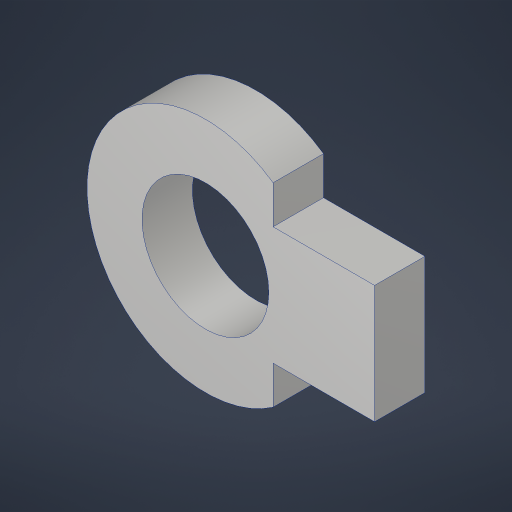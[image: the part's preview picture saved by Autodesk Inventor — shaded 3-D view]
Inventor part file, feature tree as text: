
AUTODESK INVENTOR PART (.ipt)
format: ipt  version: 2023.4 (Build 274418000, 418)  size: 176,640 bytes
history: native  units: in
note: dims shown in document units (in); Inventor stores cm internally (conversion verified against a paired STEP export)
features: extrude x1, sketch x1
ambient origin geometry x8: Origin, YZ Plane, XZ Plane, XY Plane, X Axis, Y Axis, Z Axis, Center Point
bodies: Solid1 (feature_tree)
feature tree (2):
  extrude  "Extrusion1"  Depth=0.745in
  sketch  "Sketch1"  dims[d0=1.875in d1=3.5in d2=1.745in d3=1.5in d4=1.0in d5=0.745in d6=0.0in]
